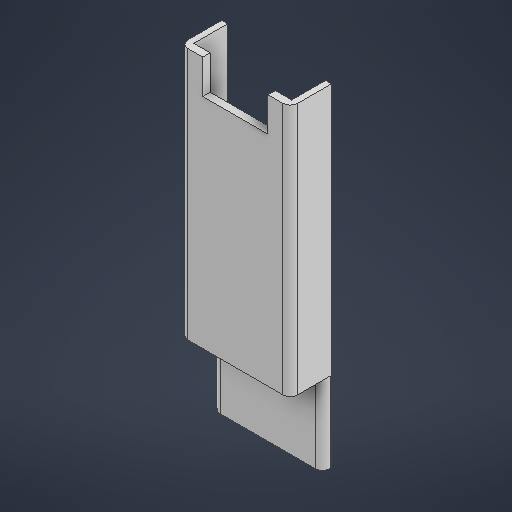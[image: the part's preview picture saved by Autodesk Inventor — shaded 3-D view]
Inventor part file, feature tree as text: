
AUTODESK INVENTOR PART (.ipt)
format: ipt  version: 2025 (Build 290162000, 162)  size: 278,528 bytes
history: native  units: in
note: dims shown in document units (in); Inventor stores cm internally (conversion verified against a paired STEP export)
features: sketch x6, extrude x5, chamfer x1, fillet x1
ambient origin geometry x8: Origin, YZ Plane, XZ Plane, XY Plane, X Axis, Y Axis, Z Axis, Center Point
bodies: Solid1 (feature_tree)
feature tree (13):
  extrude  "Extrusion1"  Depth=6.6929in
  extrude  "Extrusion2"  Depth=0.1969in
  extrude  "Extrusion3"  Depth=0.1575in TaperAngle=0.0deg
  extrude  "Extrusion4"  Depth=1.7323in
  chamfer  "Chamfer1"  Distance=0.8989in
  extrude  "Extrusion5"  Depth=0.2362in
  fillet  "Fillet1"  Radius=2.126in
  sketch  "Sketch1"  dims[d0=2.9134in d1=6.6929in]
  sketch  "Sketch2"  dims[d5=2.0472in d6=0.1575in d7=0.0in]
  sketch  "Sketch3"  dims[d8=0.1575in d9=1.7323in]
  sketch  "Sketch4"  dims[d10=0.9055in]
  sketch  "Sketch5"  dims[d12=0.1575in d13=0.8989in d14=0.0in d15=0.2362in d16=2.126in d17=0.0in d18=2.056in d19=0.2165in d20=0.2165in d21=2.9134in d23=4.3504in d24=90.0deg d25=0.187in d26=0.5906in d27=1.9685in d29=0.7874in d30=0.3937in d32=0.3937in d34=0.1969in d35=0.0in d36=0.3937in d37=0.0787in d38=0.1632in d39=0.2028in d40=0.0197in d41=0.1969in]
  sketch  "Sketch Rectangular Pattern1"  dims[d2=0.1969in d3=0.0in d4=0.187in]
